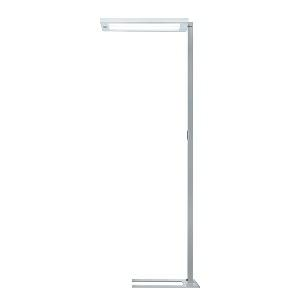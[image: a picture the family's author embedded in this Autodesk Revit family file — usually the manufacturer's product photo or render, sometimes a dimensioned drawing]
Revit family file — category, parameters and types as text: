
# Revit family: lavigo_-_dps_15000_840_r_g2a_00808521_6160
name_source: partatom
category: Lighting Fixtures
units: mm (PartAtom-declared; Revit-internal decimal feet)

## family parameters
Cut with Voids When Loaded = No
Host = Face
Light Source = No
Part Type = Normal
Room Calculation Point = No
Round Connector Dimension = Use Diameter
Shared = No

## types (1)
- LAVIGO - DPS 15000/840/R/G2A (1 x LED, 15250 lm, 4000K)
    Apparent Load = 105 VA
    Approval mark = CE
    CIE Flux Codes = 60 87 97 11 100
    Color Rendering = 80-89
    Color Temperature = 4000K
    Control Gear = Electronic ballast
    Default Elevation = 1800 mm
    Description = DPS 15000/840/R/G2A|Free-standing luminaire|light source: LED|work equipment: Electronic ballast|connected load: 220-240 V, 50/60 Hz|Power consumption: approx. 105 W|standby: approx. 0,50|power factor: approx. 0,965|luminous flux: 15250 lm|luminous efficacy: 145 lm/W|light distribution: Direct/indirect|direct ratio: approx. 12 %|colour temperature: Cold white, ca. 4000 K|color rendering index (CRI): >= 80|chromaticity tolerance:  3 SDCM|technology: Presence and daylight sensor control (PIR)|operation: Multi-function switch|luminaire body|material: Steel/plastic|surface: Painted|colour: Silver metallic|lamp cover: Acrylic (PMMA), Satine|tubular section|material: Steel tube|surface: Painted|Form: Tubular section upright|colour of tubular section: Silver metallic|luminaire base|Form: C-form flat|weight (net): approx. 19.7 kg|mains lead: 3.00 m Mains plug CEE 7/VII|Fastening: Floor standing base|decorative contrast side parts: Flint grey|glare control: Prism aperture|luminance(L65): <= 3000 cd/m|unified glare rating(4H 8H): <=  16|special features: Luminaire head detachable, Asymmetric radiation, Cradle to Cradle Certified TM, Direct light component with edge light and light-guide technology for homogenous light exit, Flicker-free, Integrated light and presence sensor PIR, Retrofittable with TALK module, Separated, direct and indirect light individually adjustable|
    Height = 36 mm
    Lamp = 1 x LED
    Lamp Light Flux = 15250 lm
    Lamp count = 1
    Length = 675 mm
    Luminous efficacy = 145 lm/W
    Manufacturer = Waldmann
    ModVariant = No
    Model = 00808521
    Mounting Place = Floor
    Mounting Type = Freestanding
    Number of Poles = 1
    OnlyDefault = Yes
    Power Factor = 1
    Product Name = LAVIGO - DPS 15000/840/R/G2A
    Product group = Free standing luminaire
    ProductGroupID = 13
    Protection Class = Protection class I
    Protection Degree = IP 20
    RLX_Detail_Level = 1
    RLX_Emergency_Light_Flux = 0 lm
    RLX_Emergency_Type = 0
    RLX_Emergency_Type_DB = No
    RlxData = <blob elided: 42309 chars, md5=a7c66f1c>
    Socket = socket
    Standby Power = 0 W
    System Light Flux = 15250 lm
    System Power = 105 W
    Type Comments = Product without accessories
    Type Image = 121695000-00625713.jpg
    URL = http://relux.com
    VarID = ---
    Voltage = 0 V
    Weight = 0.00 kg
    Width = 320 mm

## geometry (parser evidence)
native form markers: Blend x4, Sweep x17
no freeform markers — native parametric forms only
